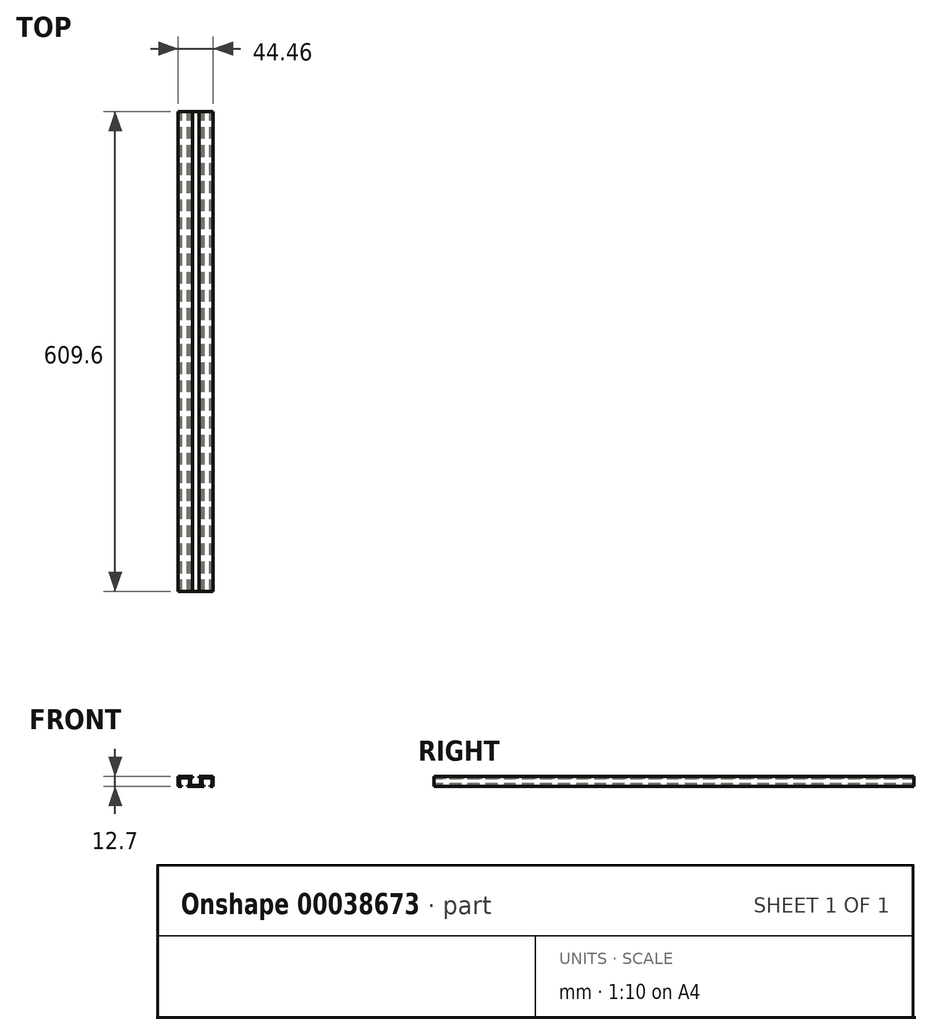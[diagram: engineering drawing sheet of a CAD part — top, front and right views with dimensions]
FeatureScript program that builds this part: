
annotation { "Feature Type Name" : "Feature", "Feature Type Description" : "" }
export const myFeature = defineFeature(function(context is Context, id is Id, definition is map)
    precondition{}
    {
        {
            var Q0;
            Q0=qCreatedBy(makeId("Front.planeOp"),FACE);
            var sketch = newSketch(context, id + "F0", { "sketchPlane" : qUnion([Q0])});
            skLineSegment(sketch, "E0", {"start": v(0, 0) * mm, "end": v(14.29, 0) * mm});
            skLineSegment(sketch, "E1", {"start": v(14.29, 0) * mm, "end": v(14.29, 1.59) * mm});
            skLineSegment(sketch, "E2", {"start": v(14.29, 1.59) * mm, "end": v(7.94, 1.59) * mm});
            skLineSegment(sketch, "E3", {"start": v(7.94, 1.59) * mm, "end": v(7.94, 11.11) * mm});
            skLineSegment(sketch, "E4", {"start": v(7.94, 11.11) * mm, "end": v(14.29, 11.11) * mm});
            skLineSegment(sketch, "E5", {"start": v(14.29, 11.11) * mm, "end": v(14.29, 12.7) * mm});
            skLineSegment(sketch, "E6", {"start": v(14.29, 12.7) * mm, "end": v(0, 12.7) * mm});
            skLineSegment(sketch, "E7", {"start": v(0, 12.7) * mm, "end": v(0, 11.11) * mm});
            skLineSegment(sketch, "E8", {"start": v(0, 11.11) * mm, "end": v(6.35, 11.11) * mm});
            skLineSegment(sketch, "E9", {"start": v(6.35, 11.11) * mm, "end": v(6.35, 1.59) * mm});
            skLineSegment(sketch, "E10", {"start": v(6.35, 1.59) * mm, "end": v(0, 1.59) * mm});
            skLineSegment(sketch, "E11", {"start": v(0, 1.59) * mm, "end": v(0, 0) * mm});
            skLineSegment(sketch, "E12", {"start": v(6.35, 6.35) * mm, "end": v(7.94, 6.35) * mm, "construction": true});
            skLineSegment(sketch, "E13", {"start": v(7.14, 6.35) * mm, "end": v(7.14, 0) * mm, "construction": true});
            skLineSegment(sketch, "E14", {"start": v(7.14, 6.35) * mm, "end": v(7.14, 12.7) * mm, "construction": true});
            skLineSegment(sketch, "E15", {"start": v(10.32, 1.59) * mm, "end": v(10.32, 0) * mm});
            skLineSegment(sketch, "E16", {"start": v(3.97, 11.11) * mm, "end": v(3.97, 12.7) * mm});
            skSolve(sketch);
        }
        {
            var Q0;
            {var subQ3=sQuery(id+"F0.wireOp",EDGE,"E3");Q0=makeQuery(id+"F0.imprint","IMPRINT",FACE,{"disambiguationData":[TD([[makeQuery(id+"F0.imprint","IMPRINT",EDGE,{"derivedFrom":subQ3}),1.0]])]});}
            var Q1;
            Q1=sQuery(id+"F0.wireOp",EDGE,"E14");
            var Q2;
            Q2=sQuery(id+"F0.wireOp",EDGE,"E13");
            var Q3;
            Q3=sQuery(id+"F0.wireOp",EDGE,"E12");
            extrude(context, id + "F1", {"entities" : qUnion([Q0]), "surfaceEntities" : qUnion([Q1, Q2, Q3]), "depth" : 609.6 * mm});
        }
        {
            var Q0;
            Q0=makeQuery(id+"F1.opExtrude","SWEPT_EDGE",EDGE,{"disambiguationData":[OSD([sQuery(id+"F0.wireOp",EDGE,"E9"),sQuery(id+"F0.wireOp",EDGE,"E10")])]});
            var Q1;
            Q1=makeQuery(id+"F1.opExtrude","SWEPT_EDGE",EDGE,{"disambiguationData":[OSD([sQuery(id+"F0.wireOp",EDGE,"E3"),sQuery(id+"F0.wireOp",EDGE,"E4")])]});
            chamfer(context, id + "F2", {"entities" : qUnion([Q0, Q1]), "width" : 1.59 * mm, "tangentPropagation" : true});
        }
        {
            var Q0;
            Q0=makeQuery(id+"F1.opExtrude","SWEPT_BODY",BODY,{"disambiguationData":[OSD([sQuery(id+"F0.wireOp",EDGE,"E0"),sQuery(id+"F0.wireOp",EDGE,"E2"),sQuery(id+"F0.wireOp",EDGE,"E3"),sQuery(id+"F0.wireOp",EDGE,"E4"),sQuery(id+"F0.wireOp",EDGE,"E5"),sQuery(id+"F0.wireOp",EDGE,"E6"),sQuery(id+"F0.wireOp",EDGE,"E8"),sQuery(id+"F0.wireOp",EDGE,"E9"),sQuery(id+"F0.wireOp",EDGE,"E10"),sQuery(id+"F0.wireOp",EDGE,"E11"),sQuery(id+"F0.wireOp",EDGE,"E15"),sQuery(id+"F0.wireOp",EDGE,"E16")])]});
            var Q1;
            Q1=makeQuery(id+"F1.opExtrude","SWEPT_FACE",FACE,{"disambiguationData":[OSD([sQuery(id+"F0.wireOp",EDGE,"E5")])]});
            mirror(context, id + "F3", {"operationType" : NewBodyOperationType.ADD, "entities" : qUnion([Q0]), "mirrorPlane" : qUnion([Q1])});
        }
        {
            var Q0;
            Q0=makeQuery(id+"F1.opExtrude","SWEPT_BODY",BODY,{"disambiguationData":[OSD([sQuery(id+"F0.wireOp",EDGE,"E0"),sQuery(id+"F0.wireOp",EDGE,"E2"),sQuery(id+"F0.wireOp",EDGE,"E3"),sQuery(id+"F0.wireOp",EDGE,"E4"),sQuery(id+"F0.wireOp",EDGE,"E5"),sQuery(id+"F0.wireOp",EDGE,"E6"),sQuery(id+"F0.wireOp",EDGE,"E8"),sQuery(id+"F0.wireOp",EDGE,"E9"),sQuery(id+"F0.wireOp",EDGE,"E10"),sQuery(id+"F0.wireOp",EDGE,"E11"),sQuery(id+"F0.wireOp",EDGE,"E15"),sQuery(id+"F0.wireOp",EDGE,"E16")])]});
            var Q1;
            Q1=makeQuery(id+"F3.opPattern","COPY",FACE,{"derivedFrom":makeQuery(id+"F1.opExtrude","SWEPT_FACE",FACE,{"disambiguationData":[OSD([sQuery(id+"F0.wireOp",EDGE,"E11")])]}),"instanceName":"1"});
            mirror(context, id + "F4", {"operationType" : NewBodyOperationType.ADD, "entities" : qUnion([Q0]), "mirrorPlane" : qUnion([Q1])});
        }
        {
            var Q0;
            {var subQ0=makeQuery(id+"F1.opExtrude","CAP_FACE",FACE,{"disambiguationData":[OSD([sQuery(id+"F0.wireOp",EDGE,"E0"),sQuery(id+"F0.wireOp",EDGE,"E2"),sQuery(id+"F0.wireOp",EDGE,"E3"),sQuery(id+"F0.wireOp",EDGE,"E4"),sQuery(id+"F0.wireOp",EDGE,"E5"),sQuery(id+"F0.wireOp",EDGE,"E6"),sQuery(id+"F0.wireOp",EDGE,"E8"),sQuery(id+"F0.wireOp",EDGE,"E9"),sQuery(id+"F0.wireOp",EDGE,"E10"),sQuery(id+"F0.wireOp",EDGE,"E11"),sQuery(id+"F0.wireOp",EDGE,"E15"),sQuery(id+"F0.wireOp",EDGE,"E16")])],"isStart":false});var subQ1=makeQuery(id+"F3.boolean.opBoolean","MERGE",FACE,{"derivedFrom":[subQ0,makeQuery(id+"F3.opPattern","COPY",FACE,{"derivedFrom":subQ0,"instanceName":"1"})]});Q0=makeQuery(id+"F4.boolean.opBoolean","MERGE",FACE,{"derivedFrom":[subQ1,makeQuery(id+"F4.opPattern","COPY",FACE,{"derivedFrom":subQ1,"instanceName":"1"})]});}
            var sketch = newSketch(context, id + "F5", { "sketchPlane" : qUnion([Q0])});
            skLineSegment(sketch, "E17", {"start": v(22.23, 12.7) * mm, "end": v(57.15, 12.7) * mm});
            skLineSegment(sketch, "E18", {"start": v(57.15, 12.7) * mm, "end": v(57.15, 0) * mm});
            skLineSegment(sketch, "E19", {"start": v(57.15, 0) * mm, "end": v(22.23, 0) * mm});
            skLineSegment(sketch, "E20", {"start": v(22.23, 12.7) * mm, "end": v(22.23, 0) * mm});
            skSolve(sketch);
        }
        {
            var Q0;
            Q0=qSketchRegion(id+"F5",true);
            extrude(context, id + "F6", {"entities" : qUnion([Q0]), "operationType" : NewBodyOperationType.REMOVE, "endBound" : BoundingType.THROUGH_ALL, "oppositeDirection" : true, "depth" : 25.4 * mm});
        }
        {
            var Q0;
            Q0=makeQuery(id+"F1.opExtrude","SWEPT_BODY",BODY,{"disambiguationData":[OSD([sQuery(id+"F0.wireOp",EDGE,"E0"),sQuery(id+"F0.wireOp",EDGE,"E2"),sQuery(id+"F0.wireOp",EDGE,"E3"),sQuery(id+"F0.wireOp",EDGE,"E4"),sQuery(id+"F0.wireOp",EDGE,"E5"),sQuery(id+"F0.wireOp",EDGE,"E6"),sQuery(id+"F0.wireOp",EDGE,"E8"),sQuery(id+"F0.wireOp",EDGE,"E9"),sQuery(id+"F0.wireOp",EDGE,"E10"),sQuery(id+"F0.wireOp",EDGE,"E11"),sQuery(id+"F0.wireOp",EDGE,"E15"),sQuery(id+"F0.wireOp",EDGE,"E16")])]});
            var Q1;
            Q1=makeQuery(id+"F1.opExtrude","SWEPT_FACE",FACE,{"disambiguationData":[OSD([sQuery(id+"F0.wireOp",EDGE,"E11")])]});
            mirror(context, id + "F7", {"operationType" : NewBodyOperationType.ADD, "entities" : qUnion([Q0]), "mirrorPlane" : qUnion([Q1])});
        }
    });
